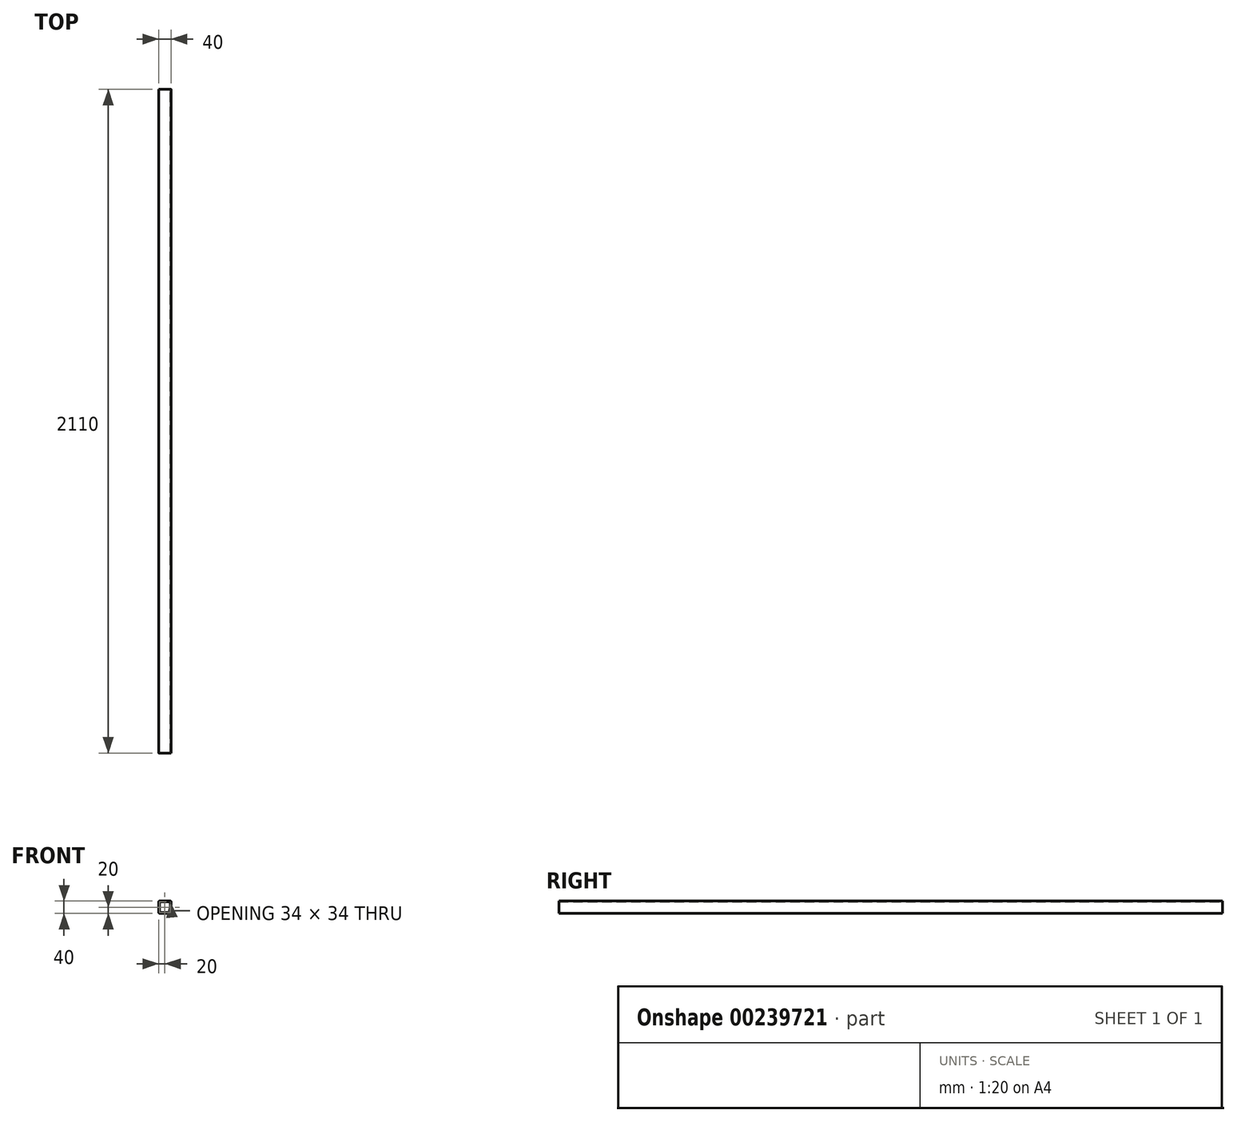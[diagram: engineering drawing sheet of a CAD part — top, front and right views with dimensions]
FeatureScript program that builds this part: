
annotation { "Feature Type Name" : "Feature", "Feature Type Description" : "" }
export const myFeature = defineFeature(function(context is Context, id is Id, definition is map)
    precondition{}
    {
        {
            var Q0;
            Q0=qCreatedBy(makeId("Front.planeOp"),FACE);
            var sketch = newSketch(context, id + "F0", { "sketchPlane" : qUnion([Q0])});
            skLineSegment(sketch, "E0.bottom", {"start": v(16, 20) * mm, "end": v(-16, 20) * mm});
            skLineSegment(sketch, "E0.top", {"start": v(16, -20) * mm, "end": v(-16, -20) * mm});
            skLineSegment(sketch, "E0.left", {"start": v(20, 16) * mm, "end": v(20, -16) * mm});
            skLineSegment(sketch, "E0.right", {"start": v(-20, 16) * mm, "end": v(-20, -16) * mm});
            skPoint(sketch, "E0.middle", {"position": v(0, 0) * mm});
            skPoint(sketch, "E1.visualSharp", {"position": v(-20, 20) * mm});
            skArc(sketch, "E1.filletArc", {"start": v(-16, 20) * mm, "mid": v(-18.83, 18.83) * mm, "end": v(-20, 16) * mm});
            skPoint(sketch, "E2.visualSharp", {"position": v(20, 20) * mm});
            skArc(sketch, "E2.filletArc", {"start": v(20, 16) * mm, "mid": v(18.83, 18.83) * mm, "end": v(16, 20) * mm});
            skPoint(sketch, "E3.visualSharp", {"position": v(20, -20) * mm});
            skArc(sketch, "E3.filletArc", {"start": v(16, -20) * mm, "mid": v(18.83, -18.83) * mm, "end": v(20, -16) * mm});
            skPoint(sketch, "E4.visualSharp", {"position": v(-20, -20) * mm});
            skArc(sketch, "E4.filletArc", {"start": v(-20, -16) * mm, "mid": v(-18.83, -18.83) * mm, "end": v(-16, -20) * mm});
            skLineSegment(sketch, "E5.0", {"start": v(16, 17) * mm, "end": v(-16, 17) * mm});
            skArc(sketch, "E5.1", {"start": v(17, 16) * mm, "mid": v(16.7, 16.7) * mm, "end": v(16, 17) * mm});
            skArc(sketch, "E5.2", {"start": v(-16, 17) * mm, "mid": v(-16.7, 16.7) * mm, "end": v(-17, 16) * mm});
            skLineSegment(sketch, "E5.3", {"start": v(17, 16) * mm, "end": v(17, -16) * mm});
            skLineSegment(sketch, "E5.4", {"start": v(-17, 16) * mm, "end": v(-17, -16) * mm});
            skArc(sketch, "E5.5", {"start": v(-17, -16) * mm, "mid": v(-16.7, -16.7) * mm, "end": v(-16, -17) * mm});
            skLineSegment(sketch, "E5.6", {"start": v(16, -17) * mm, "end": v(-16, -17) * mm});
            skArc(sketch, "E5.7", {"start": v(16, -17) * mm, "mid": v(16.7, -16.7) * mm, "end": v(17, -16) * mm});
            skSolve(sketch);
        }
        {
            var Q0;
            Q0=makeQuery(id+"F0.imprint","IMPRINT",FACE,{"disambiguationData":[TD([[makeQuery(id+"F0.imprint","IMPRINT",EDGE,{"derivedFrom":sQuery(id+"F0.wireOp",EDGE,"E0.bottom")}),1.0]])]});
            extrude(context, id + "F1", {"entities" : qUnion([Q0]), "depth" : 2110 * mm});
        }
    });
